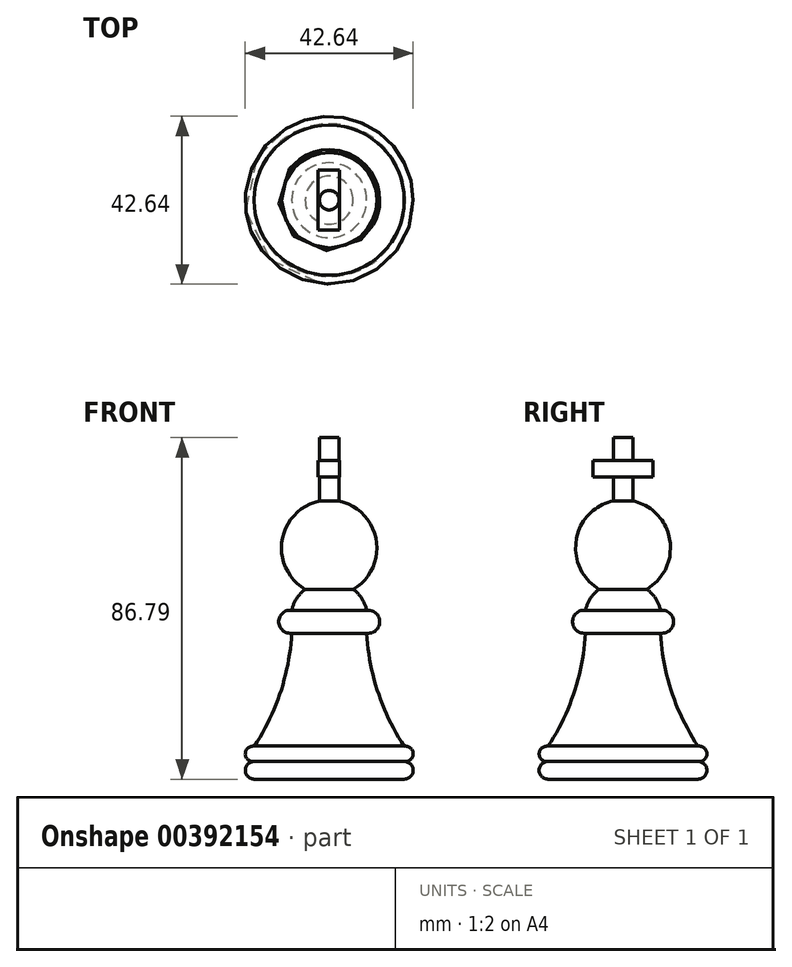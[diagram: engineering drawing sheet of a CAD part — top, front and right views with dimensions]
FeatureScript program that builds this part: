
annotation { "Feature Type Name" : "Feature", "Feature Type Description" : "" }
export const myFeature = defineFeature(function(context is Context, id is Id, definition is map)
    precondition{}
    {
        {
            var Q0;
            Q0=qCreatedBy(makeId("Front.planeOp"),FACE);
            var sketch = newSketch(context, id + "F0", { "sketchPlane" : qUnion([Q0])});
            skLineSegment(sketch, "E0", {"start": v(0, 33.3) * mm, "end": v(0, -42.9) * mm});
            skLineSegment(sketch, "E1", {"start": v(0, -42.9) * mm, "end": v(-19.05, -42.9) * mm});
            skArc(sketch, "E2", {"start": v(-19.05, -38.4) * mm, "mid": v(-21.3, -40.65) * mm, "end": v(-19.05, -42.9) * mm});
            skArc(sketch, "E3", {"start": v(-19.05, -34.52) * mm, "mid": v(-21.32, -36.46) * mm, "end": v(-19.05, -38.4) * mm});
            skArc(sketch, "E4", {"start": v(-19.05, -34.52) * mm, "mid": v(-12.38, -20.8) * mm, "end": v(-9.52, -5.8) * mm});
            skPoint(sketch, "E4.endSnap0", {"position": v(-9.52, -42.9) * mm});
            skArc(sketch, "E5", {"start": v(-9.53, 0) * mm, "mid": v(-12.84, -2.9) * mm, "end": v(-9.52, -5.8) * mm});
            skArc(sketch, "E6", {"start": v(-6.1, 5.34) * mm, "mid": v(-8.3, 2.98) * mm, "end": v(-9.53, 0) * mm});
            skArc(sketch, "E7", {"start": v(-2.48, 27.8) * mm, "mid": v(-11.97, 17.8) * mm, "end": v(-6.1, 5.34) * mm});
            skLineSegment(sketch, "E8", {"start": v(-2.48, 27.8) * mm, "end": v(-2.48, 43.88) * mm});
            skLineSegment(sketch, "E9", {"start": v(-2.48, 43.88) * mm, "end": v(0, 43.88) * mm});
            skLineSegment(sketch, "E10", {"start": v(0, 43.88) * mm, "end": v(0, 33.3) * mm});
            skPoint(sketch, "E11.orphan", {"position": v(0, 28.07) * mm});
            skSolve(sketch);
        }
        {
            var Q0;
            Q0 = qSketchRegion(id + "F0", true);
            var Q1;
            Q1=sQuery(id+"F0.wireOp",EDGE,"E0");
            revolve(context, id + "F1", {"entities" : qUnion([Q0]), "axis" : qUnion([Q1]), "revolveType" : RevolveType.FULL});
        }
        {
            var Q0;
            Q0=qCreatedBy(makeId("Front.planeOp"),FACE);
            var sketch = newSketch(context, id + "F2", { "sketchPlane" : qUnion([Q0])});
            skLineSegment(sketch, "E12.bottom", {"start": v(-2.9, 38.07) * mm, "end": v(2.58, 38.07) * mm});
            skLineSegment(sketch, "E12.top", {"start": v(-2.9, 33.88) * mm, "end": v(2.58, 33.88) * mm});
            skLineSegment(sketch, "E12.left", {"start": v(-2.9, 38.07) * mm, "end": v(-2.9, 33.88) * mm});
            skLineSegment(sketch, "E12.right", {"start": v(2.58, 38.07) * mm, "end": v(2.58, 33.88) * mm});
            skSolve(sketch);
        }
        {
            var Q0;
            Q0 = qSketchRegion(id + "F2", true);
            extrude(context, id + "F3", {"entities" : qUnion([Q0]), "operationType" : NewBodyOperationType.ADD, "depth" : 7.62 * mm});
        }
        {
            var Q0;
            Q0 = qSketchRegion(id + "F2", true);
            extrude(context, id + "F4", {"entities" : qUnion([Q0]), "operationType" : NewBodyOperationType.ADD, "oppositeDirection" : true, "depth" : 7.62 * mm});
        }
    });
